# Revit family: 100-LAVAPLATOS SOBREPONER 80X50 DERECHO PARA GRIF COMBINACIÓN
name_source: partatom
category: Aparatos sanitarios
units: mm (PartAtom-declared; Revit-internal decimal feet)

## family parameters
Compartido = No
Corte con vacíos al cargar = No
Cota de conector redondo = Radio de uso
Número OmniClass = 23.45.05.14.21.11
Punto de cálculo de habitación = No
Se basa en plano de trabajo = No
Siempre vertical = Sí
Tipo de pieza = Normal
Título OmniClass = Bath/Shower Units

## types (1)
- LAVAPLATOS SOBREPONER 80X50 DERECHO PARA GRIF COMBINACIÓN
    ACERO INOXIDABLE = Acero inoxidable
    ALTURA COLOCACION = 80 cm
    CWFU = 3
    Cold Water Radius = 8 mm
    Elevación por defecto = 0 cm
    F_Alto = 16 cm
    F_Ancho = 80 cm
    F_Color = Acero inoxidable
    F_Descripción = Lavaplatos con escurridor derecho para instalación de grifería combinación 8". Fabricado en acero inoxidable de 0,6 mm de espesor
    F_Peso = 0.00 kgf
    F_Productos incluidos = Desagüe de 70 mm y sifón completo
    F_Productos necesarios para instalación = Griferia combinación 8"
    F_Profundidad = 50 cm
    F_SKU = JHCL00006041CJ
    F_Tipo de instalación = Sobre mueble o cubierta
    F_Tolerancia dimensional = 0,5 cm máx
    HWFU = 3
    Nota clave = Falta borde trasero
    Sanitary Radius = 20 mm
    URL = https://www.fanaloza.cl
    WFU = 2

## geometry (parser evidence)
native form markers: Sweep x9
no freeform markers — native parametric forms only
